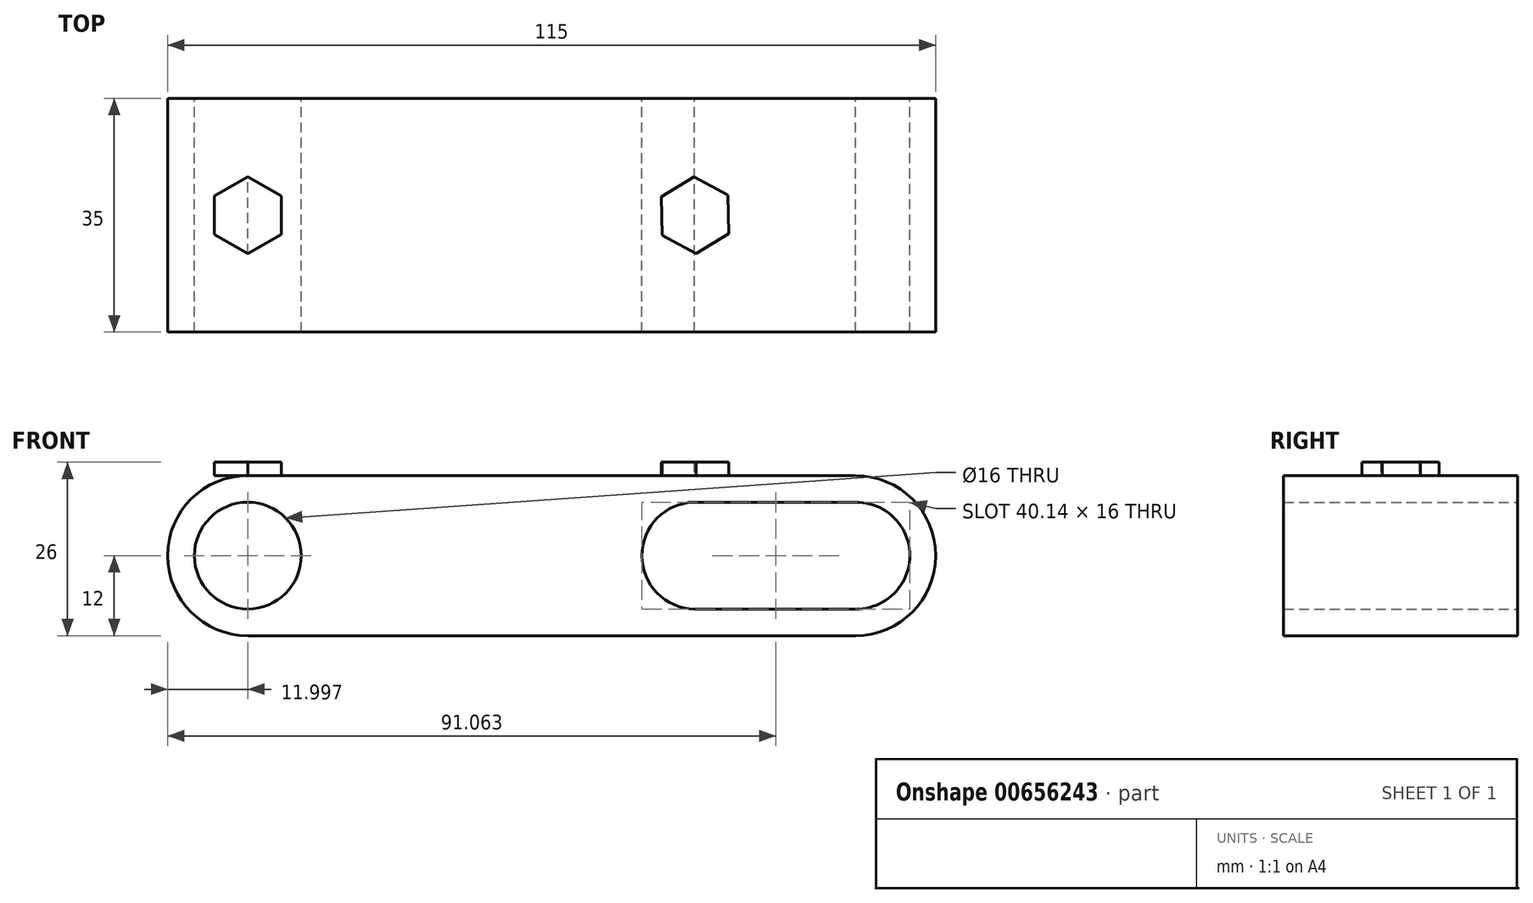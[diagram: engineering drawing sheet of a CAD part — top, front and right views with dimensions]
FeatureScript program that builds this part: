
annotation { "Feature Type Name" : "Feature", "Feature Type Description" : "" }
export const myFeature = defineFeature(function(context is Context, id is Id, definition is map)
    precondition{}
    {
        {
            var Q0;
            Q0=qCreatedBy(makeId("Front.planeOp"),FACE);
            var sketch = newSketch(context, id + "F0", { "sketchPlane" : qUnion([Q0])});
            skCircle(sketch, "E0", {"center": v(-62, 0) * mm, "radius": 8 * mm});
            skArc(sketch, "E1", {"start": v(29, -12) * mm, "mid": v(41, 0) * mm, "end": v(29, 12) * mm});
            skLineSegment(sketch, "E2", {"start": v(-62.01, -12) * mm, "end": v(29, -12) * mm});
            skLineSegment(sketch, "E3", {"start": v(29, 12) * mm, "end": v(-62, 12) * mm});
            skArc(sketch, "E4", {"start": v(-62, 12) * mm, "mid": v(-74, 0) * mm, "end": v(-62.01, -12) * mm});
            skPoint(sketch, "E5.startSnap0", {"position": v(-74, 0) * mm});
            skArc(sketch, "E6", {"start": v(4.88, 8) * mm, "mid": v(-3, 0) * mm, "end": v(4.88, -8) * mm});
            skArc(sketch, "E7", {"start": v(29, -8) * mm, "mid": v(37.13, 0) * mm, "end": v(29, 8) * mm});
            skLineSegment(sketch, "E8", {"start": v(4.88, 8) * mm, "end": v(29, 8) * mm});
            skLineSegment(sketch, "E9", {"start": v(29, -8) * mm, "end": v(4.88, -8) * mm});
            skSolve(sketch);
        }
        {
            var Q0;
            Q0=makeQuery(id+"F0.imprint","IMPRINT",FACE,{"disambiguationData":[TD([[makeQuery(id+"F0.imprint","IMPRINT",EDGE,{"derivedFrom":sQuery(id+"F0.wireOp",EDGE,"E0")}),-1.0]])]});
            extrude(context, id + "F1", {"entities" : qUnion([Q0]), "depth" : 35 * mm, "offsetDistance" : 25.4 * mm});
        }
        {
            var Q0;
            Q0=makeQuery(id+"F1.opExtrude","SWEPT_FACE",FACE,{"disambiguationData":[OSD([sQuery(id+"F0.wireOp",EDGE,"E3")])]});
            var sketch = newSketch(context, id + "F2", { "sketchPlane" : qUnion([Q0])});
            skCircle(sketch, "E10.cCircle", {"center": v(4.96, -17.5) * mm, "radius": 5 * mm, "construction": true});
            skPoint(sketch, "E10.cCircle.centerSnap0", {"position": v(29, -17.5) * mm});
            skLineSegment(sketch, "E10.0", {"start": v(4.82, -11.73) * mm, "end": v(9.9, -14.49) * mm});
            skLineSegment(sketch, "E10.1", {"start": v(9.9, -14.49) * mm, "end": v(10.04, -20.26) * mm});
            skLineSegment(sketch, "E10.2", {"start": v(10.04, -20.26) * mm, "end": v(5.11, -23.27) * mm});
            skLineSegment(sketch, "E10.3", {"start": v(5.11, -23.27) * mm, "end": v(0.04, -20.51) * mm});
            skLineSegment(sketch, "E10.4", {"start": v(0.04, -20.51) * mm, "end": v(-0.1, -14.74) * mm});
            skLineSegment(sketch, "E10.5", {"start": v(-0.1, -14.74) * mm, "end": v(4.82, -11.73) * mm});
            skPoint(sketch, "E10.0.midPoint", {"position": v(7.36, -13.1) * mm});
            skPoint(sketch, "E11", {"position": v(40.96, -17.5) * mm});
            skCircle(sketch, "E12.cCircle", {"center": v(-62, -17.5) * mm, "radius": 5 * mm, "construction": true});
            skLineSegment(sketch, "E12.0", {"start": v(-57, -14.61) * mm, "end": v(-57, -20.39) * mm});
            skLineSegment(sketch, "E12.1", {"start": v(-57, -20.39) * mm, "end": v(-62, -23.27) * mm});
            skLineSegment(sketch, "E12.2", {"start": v(-62, -23.27) * mm, "end": v(-67, -20.39) * mm});
            skLineSegment(sketch, "E12.3", {"start": v(-67, -20.39) * mm, "end": v(-67, -14.61) * mm});
            skLineSegment(sketch, "E12.4", {"start": v(-67, -14.61) * mm, "end": v(-62, -11.73) * mm});
            skLineSegment(sketch, "E12.5", {"start": v(-62, -11.73) * mm, "end": v(-57, -14.61) * mm});
            skPoint(sketch, "E12.0.midPoint", {"position": v(-57, -17.5) * mm});
            skSolve(sketch);
        }
        {
            var Q0;
            Q0 = qSketchRegion(id + "F2", true);
            extrude(context, id + "F3", {"entities" : qUnion([Q0]), "operationType" : NewBodyOperationType.ADD, "depth" : 2 * mm, "offsetDistance" : 25.4 * mm});
        }
    });
